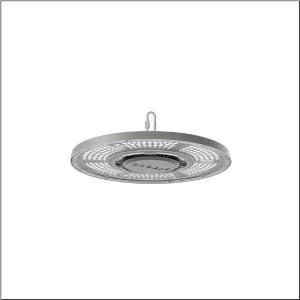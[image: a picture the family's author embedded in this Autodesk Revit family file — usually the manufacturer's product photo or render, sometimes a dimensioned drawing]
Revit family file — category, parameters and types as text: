
# Revit family: highbay_31-s_51hc427a4jmb
name_source: partatom
category: Lighting Fixtures
units: mm (PartAtom-declared; Revit-internal decimal feet)

## family parameters
Cut with Voids When Loaded = No
Host = Face
Light Source = No
Part Type = Normal
Room Calculation Point = No
Round Connector Dimension = Use Diameter
Shared = No

## types (1)
- Highbay 31-S (1 x LED, 20000 lm, 134 W, 4000K)
    Apparent Load = 134 VA
    CIE Flux Codes = 77 99 100 100 100
    Color Rendering = 80
    Color Temperature = 4000K
    Default Elevation = 1800 mm
    Description = Highbay 31-S, LED high bay luminaire, primary light control with lens, of PC, primary optical cover: cover panel, of PC, transparent, light emission: direct distribution, primary light characteristic: rotationally symmetric, installation type: suspended mounting, surface-mounted, LED, rated luminous flux: 20.000lm, luminous efficacy: 150lm/W, light colour: 840, colour temperature: 4000K, control gear: ECG, with cable, 3x 1.0mm², free wire ends, mains connection: 220..240V, AC/DC, 0/50..60Hz, cable length: 1,5m, rated input power: 134W, housing, rotationally symmetric, of diecast aluminium, powder-coated, grey aluminium (RAL 9007), with hook on luminaire side, incl. screw, diameter: 339mm, protection rating (complete): IP65, insulation class (complete): insulation class I (protective earthing), certification: CE, ENEC, UKCA, protection symbol: D, impact resistance: IK08, permissible operating ambient temperature: -30..+45°C, standard: EN 60598-2-22, EN 60598, corresponds to IFS (International Featured Standards) requirements for safety and quality in the food industry, packaging unit: 1 piece
    Height = 141 mm
    Lamp = 1 x LED
    Lamp Light Flux = 20000 lm
    Lamp Power = 134 W
    Lamp count = 1
    Length = 339 mm
    Luminous efficacy = 149 lm/W
    Manufacturer = Siteco
    ModVariant = No
    Model = 51HC427A4JMB
    Mounting Place = Ceiling
    Mounting Type = Pendant
    Number of Poles = 1
    OnlyDefault = Yes
    Power Factor = 1
    Product Name = Highbay 31-S
    Product group = LED high bay luminaire
    ProductGroupID = 903
    Protection Class = Protection class I
    Protection Degree = IP 65
    RLX_Detail_Level = 1
    RLX_Emergency_Light_Flux = 0 lm
    RLX_Emergency_Type = 0
    RLX_Emergency_Type_DB = No
    RlxData = <blob elided: 163169 chars, md5=2e261f99>
    Socket = socket
    Standby Power = 0 W
    System Light Flux = 20000 lm
    System Power = 134 W
    Type Comments = Product without accessories
    Type Image = l_1007237.jpg
    URL = http://relux.com
    VarID = ---
    Voltage = 0 V
    Weight = 0.00 kg
    Width = 0 mm  [stored 0 ft]

note: [stored X ft] marks values corroborated as IEEE doubles in the binary element streams (Revit-internal decimal feet)

## geometry (parser evidence)
native form markers: Blend x4, Sweep x9
no freeform markers — native parametric forms only
